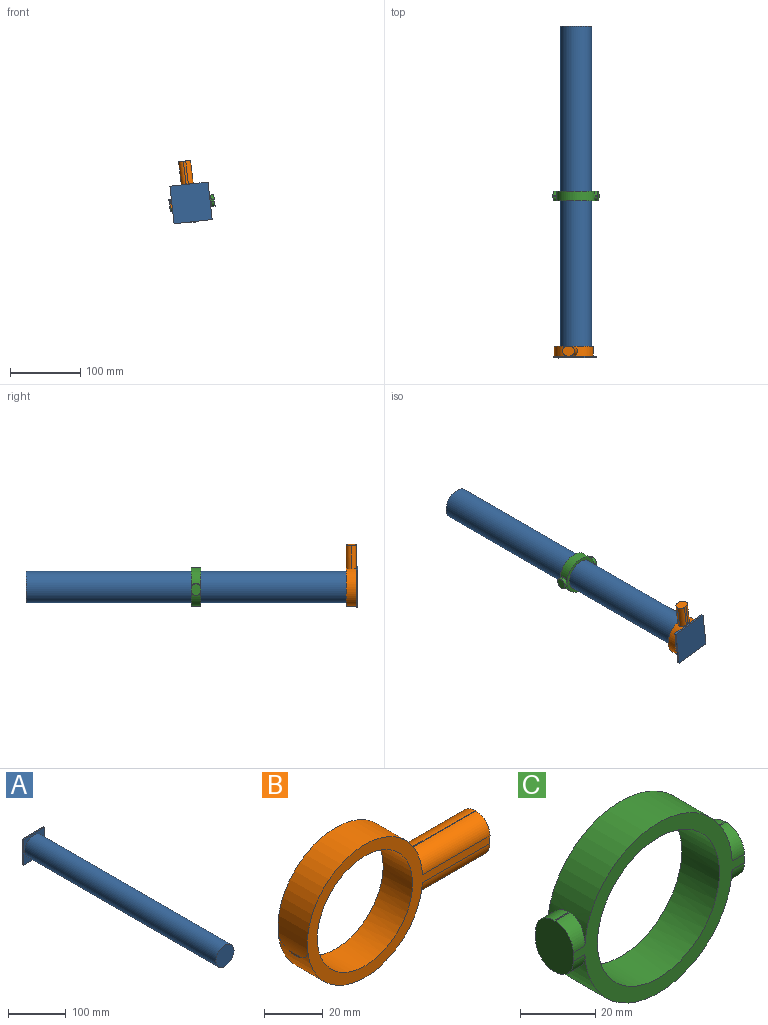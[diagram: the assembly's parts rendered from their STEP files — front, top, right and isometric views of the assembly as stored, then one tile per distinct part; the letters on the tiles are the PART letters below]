
ASSEMBLY  parts=3 mates=2
PART A: 8 faces, bbox 53.7x472.6x54.6 mm
  f0: cylinder r=22.27mm len=470mm, axis (0,1,0), area 65777.3mm2, adj f1,f7
  f1: plane 44.55x44.55mm, normal (0,-1,0), area 1558.6mm2, adj f0
  f2: plane 53.66x2.61mm, normal (0,0,-1), area 140.2mm2, adj f3,f5,f6,f7
  f3: plane 54.57x2.61mm, normal (1,0,0), area 142.6mm2, adj f2,f4,f6,f7
  f4: plane 53.66x2.61mm, normal (0,0,1), area 140.2mm2, adj f3,f5,f6,f7
  f5: plane 54.57x2.61mm, normal (-1,0,0), area 142.6mm2, adj f2,f4,f6,f7
  f6: plane 54.57x53.66mm, normal (0,1,0), area 2928.4mm2, adj f2,f3,f4,f5
  f7: plane 54.57x53.66mm, normal (0,-1,0), area 1369.7mm2, adj f0,f2,f3,f4,f5
PART B: 16 faces, bbox 87.8x14.1x55.4 mm
  f0: cylinder r=27.66mm len=55.3mm, axis (0,1,0), area 1232.3mm2, adj f1,f3,f6,f7,f8,f11,f13
  f1: plane 6.77x0.79mm, normal (-1,0,0), area 3.7mm2, adj f0,f2,f14,f15
  f2: plane 0.37x0.26mm, normal (0,0,-1), area 0.1mm2, adj f1,f3,f14,f15
  f3: cylinder r=27.66mm len=55.18mm, axis (0,1,0), area 1011.6mm2, adj f0,f2,f4,f7,f8,f10,f12,f14
  f4: plane 33.74x0.37mm, normal (0,0,-1), area 12.6mm2, adj f3,f5,f10,f12
  f5: plane 17.01x14.12mm, normal (1,0,-0.01), area 199mm2, adj f4,f6,f7,f8,f10,f11,f12,f13
  f6: plane 33.64x0.37mm, normal (0,0,1), area 12.6mm2, adj f0,f5,f11,f13
  f7: plane 87.69x55.33mm, normal (0,-1,0), area 868.5mm2, adj f0,f3,f5,f9,f12,f13
  f8: plane 87.69x55.33mm, normal (0,1,0), area 868.5mm2, adj f0,f3,f5,f9,f10,f11
  f9: cylinder r=22.86mm len=45.72mm, axis (0,1,0), area 2023.9mm2, adj f7,f8
  f10: cylinder r=6.86mm len=33.8mm, axis (1,0,0), area 357mm2, adj f3,f4,f5,f8
  f11: cylinder r=6.86mm len=33.64mm, axis (-1,0,0), area 356.1mm2, adj f0,f5,f6,f8
  f12: cylinder r=6.86mm len=33.8mm, axis (-1,0,0), area 357mm2, adj f3,f4,f5,f7
  f13: cylinder r=6.86mm len=33.64mm, axis (1,0,0), area 356.1mm2, adj f0,f5,f6,f7
  f14: cylinder r=6.86mm len=3.2mm, axis (1,0,0), area 0.6mm2, adj f1,f2,f3
  f15: cylinder r=6.86mm len=3.2mm, axis (-1,0,0), area 0.6mm2, adj f1,f2,f3
PART C: 19 faces, bbox 64.2x14.1x55.3 mm
  f0: cylinder r=27.66mm len=55.26mm, axis (0,1,0), area 1029.4mm2, adj f1,f7,f8,f9,f12,f14,f16,f18
  f1: plane 5.59x0.37mm, normal (0,0,1), area 2.1mm2, adj f0,f2,f16,f18
  f2: plane 16.53x14.09mm, normal (-1,0,0), area 192.6mm2, adj f1,f3,f8,f9,f15,f16,f17,f18
  f3: plane 5.58x0.37mm, normal (0,0,-1), area 2.1mm2, adj f2,f4,f15,f17
  f4: cylinder r=27.66mm len=55.26mm, axis (0,1,0), area 1030.2mm2, adj f3,f5,f8,f9,f11,f13,f15,f17
  f5: plane 5.79x0.37mm, normal (0,0,-1), area 2.2mm2, adj f4,f6,f11,f13
  f6: plane 16.53x14.09mm, normal (1,0,0), area 192.6mm2, adj f5,f7,f8,f9,f11,f12,f13,f14
  f7: plane 5.8x0.37mm, normal (0,0,1), area 2.2mm2, adj f0,f6,f12,f14
  f8: plane 64.18x55.33mm, normal (0,-1,0), area 787.6mm2, adj f0,f2,f4,f6,f10,f13,f14,f17
  f9: plane 64.18x55.33mm, normal (0,1,0), area 787.6mm2, adj f0,f2,f4,f6,f10,f11,f12,f15
  f10: cylinder r=22.86mm len=45.72mm, axis (0,1,0), area 2023.9mm2, adj f8,f9
  f11: cylinder r=6.86mm len=6.86mm, axis (1,0,0), area 56.2mm2, adj f4,f5,f6,f9
  f12: cylinder r=6.86mm len=6.86mm, axis (-1,0,0), area 56.3mm2, adj f0,f6,f7,f9
  f13: cylinder r=6.86mm len=6.86mm, axis (-1,0,0), area 56.2mm2, adj f4,f5,f6,f8
  f14: cylinder r=6.86mm len=6.86mm, axis (1,0,0), area 56.3mm2, adj f0,f6,f7,f8
  f15: cylinder r=6.86mm len=6.86mm, axis (1,0,0), area 54mm2, adj f2,f3,f4,f9
  f16: cylinder r=6.86mm len=6.86mm, axis (-1,0,0), area 54.1mm2, adj f0,f1,f2,f9
  f17: cylinder r=6.86mm len=6.86mm, axis (-1,0,0), area 54mm2, adj f2,f3,f4,f8
  f18: cylinder r=6.86mm len=6.86mm, axis (1,0,0), area 54.1mm2, adj f0,f1,f2,f8
PLACE A rot(axis=(-0.67,0,-0.74),180deg) t=(0,-235,0)mm
PLACE B rot(axis=(-0.66,0,-0.75),180deg) t=(-3.18,-235,0.17)mm
PLACE C rot(axis=(-0.06,0,1),180deg) t=(0,-14.09,0)mm
MATE revolute C.f10 <-> A.f0  axis (0,1,0) through (0,0,0)mm
MATE revolute B.f9 <-> A.f7  axis (0,-1,0) through (-3.18,-235,0.17)mm
